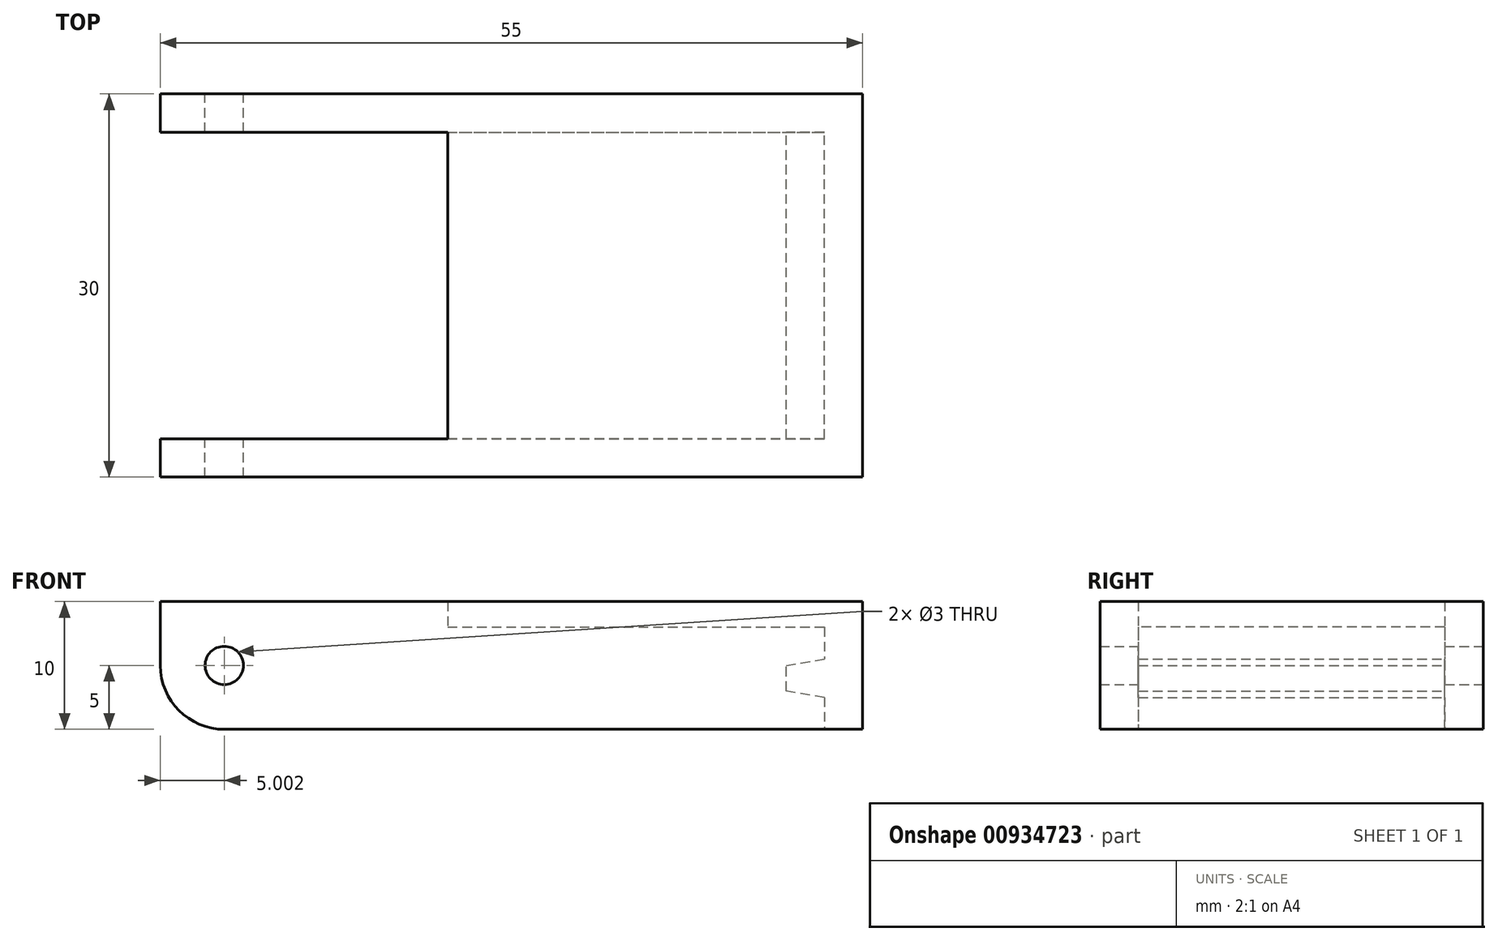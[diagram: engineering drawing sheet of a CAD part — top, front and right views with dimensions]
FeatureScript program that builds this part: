
annotation { "Feature Type Name" : "Feature", "Feature Type Description" : "" }
export const myFeature = defineFeature(function(context is Context, id is Id, definition is map)
    precondition{}
    {
        {
            var Q0;
            Q0=qCreatedBy(makeId("Top.planeOp"),FACE);
            var sketch = newSketch(context, id + "F0", { "sketchPlane" : qUnion([Q0])});
            skLineSegment(sketch, "E0", {"start": v(-28.72, -17.3) * mm, "end": v(26.28, -17.3) * mm});
            skLineSegment(sketch, "E1", {"start": v(26.28, -17.3) * mm, "end": v(26.28, 12.7) * mm});
            skLineSegment(sketch, "E2", {"start": v(26.28, 12.7) * mm, "end": v(-28.72, 12.7) * mm});
            skLineSegment(sketch, "E3", {"start": v(-28.72, 12.7) * mm, "end": v(-28.72, 9.7) * mm});
            skLineSegment(sketch, "E4", {"start": v(-28.72, 9.7) * mm, "end": v(-6.22, 9.7) * mm});
            skLineSegment(sketch, "E5", {"start": v(-6.22, 9.7) * mm, "end": v(-6.22, -14.3) * mm});
            skLineSegment(sketch, "E6", {"start": v(-6.22, -14.3) * mm, "end": v(-28.72, -14.3) * mm});
            skLineSegment(sketch, "E7", {"start": v(-28.72, -14.3) * mm, "end": v(-28.72, -17.3) * mm});
            skSolve(sketch);
        }
        {
            var Q0;
            Q0 = qSketchRegion(id + "F0", true);
            extrude(context, id + "F1", {"entities" : qUnion([Q0]), "depth" : 10 * mm, "offsetDistance" : 25 * mm});
        }
        {
            var Q0;
            Q0=makeQuery(id+"F1.opExtrude","CAP_FACE",FACE,{"disambiguationData":[OSD([sQuery(id+"F0.wireOp",EDGE,"E0"),sQuery(id+"F0.wireOp",EDGE,"E1"),sQuery(id+"F0.wireOp",EDGE,"E2"),sQuery(id+"F0.wireOp",EDGE,"E3"),sQuery(id+"F0.wireOp",EDGE,"E4"),sQuery(id+"F0.wireOp",EDGE,"E5"),sQuery(id+"F0.wireOp",EDGE,"E6"),sQuery(id+"F0.wireOp",EDGE,"E7")])],"isStart":true});
            var sketch = newSketch(context, id + "F2", { "sketchPlane" : qUnion([Q0])});
            skLineSegment(sketch, "E8.0", {"start": v(-28.72, 14.3) * mm, "end": v(26.28, 14.3) * mm, "construction": true});
            skLineSegment(sketch, "E9.0", {"start": v(26.28, -9.7) * mm, "end": v(-28.72, -9.7) * mm, "construction": true});
            skLineSegment(sketch, "E10.0", {"start": v(23.28, 17.3) * mm, "end": v(23.28, -12.7) * mm, "construction": true});
            skLineSegment(sketch, "E11.bottom", {"start": v(-6.22, 14.3) * mm, "end": v(23.28, 14.3) * mm});
            skLineSegment(sketch, "E11.top", {"start": v(-6.22, -9.7) * mm, "end": v(23.28, -9.7) * mm});
            skLineSegment(sketch, "E11.left", {"start": v(-6.22, 14.3) * mm, "end": v(-6.22, -9.7) * mm});
            skLineSegment(sketch, "E11.right", {"start": v(23.28, 14.3) * mm, "end": v(23.28, -9.7) * mm});
            skSolve(sketch);
        }
        {
            var Q0;
            Q0 = qSketchRegion(id + "F2", true);
            extrude(context, id + "F3", {"entities" : qUnion([Q0]), "operationType" : NewBodyOperationType.REMOVE, "oppositeDirection" : true, "depth" : 8 * mm, "offsetDistance" : 25 * mm});
        }
        {
            var Q0;
            Q0=makeQuery(id+"F3.boolean.opBoolean","MERGE",FACE,{"derivedFrom":[makeQuery(id+"F1.opExtrude","SWEPT_FACE",FACE,{"disambiguationData":[OSD([sQuery(id+"F0.wireOp",EDGE,"E4")])]})],"fromTools":[makeQuery(id+"F3.opExtrude","SWEPT_FACE",FACE,{"disambiguationData":[OSD([sQuery(id+"F2.wireOp",EDGE,"E11.top")])]})]});
            var sketch = newSketch(context, id + "F4", { "sketchPlane" : qUnion([Q0])});
            skLineSegment(sketch, "E12", {"start": v(23.28, 0) * mm, "end": v(17.27, 0) * mm, "construction": true});
            skLineSegment(sketch, "E13", {"start": v(23.28, 5.5) * mm, "end": v(23.28, 2.5) * mm});
            skLineSegment(sketch, "E14", {"start": v(23.28, 2.5) * mm, "end": v(20.28, 3) * mm});
            skLineSegment(sketch, "E15", {"start": v(20.28, 3) * mm, "end": v(20.28, 5) * mm});
            skLineSegment(sketch, "E16", {"start": v(20.28, 5) * mm, "end": v(23.28, 5.5) * mm});
            skSolve(sketch);
        }
        {
            var Q0;
            Q0 = qSketchRegion(id + "F4", true);
            extrude(context, id + "F5", {"entities" : qUnion([Q0]), "operationType" : NewBodyOperationType.ADD, "depth" : 24 * mm, "offsetDistance" : 25 * mm});
        }
        {
            var Q0;
            Q0=makeQuery(id+"F1.opExtrude","SWEPT_FACE",FACE,{"disambiguationData":[OSD([sQuery(id+"F0.wireOp",EDGE,"E2")])]});
            var sketch = newSketch(context, id + "F6", { "sketchPlane" : qUnion([Q0])});
            skLineSegment(sketch, "E17.bottom", {"start": v(28.72, 10) * mm, "end": v(16.6, 10) * mm, "construction": true});
            skLineSegment(sketch, "E17.top", {"start": v(28.72, 0) * mm, "end": v(16.6, 0) * mm, "construction": true});
            skLineSegment(sketch, "E17.left", {"start": v(28.72, 10) * mm, "end": v(28.72, 0) * mm, "construction": true});
            skCircle(sketch, "E18", {"center": v(23.72, 5) * mm, "radius": 1.5 * mm});
            skSolve(sketch);
        }
        {
            var Q0;
            Q0 = qSketchRegion(id + "F6", true);
            extrude(context, id + "F7", {"entities" : qUnion([Q0]), "operationType" : NewBodyOperationType.REMOVE, "oppositeDirection" : true, "depth" : 30 * mm, "offsetDistance" : 25 * mm});
        }
        {
            var Q0;
            Q0=makeQuery(id+"F1.opExtrude","CAP_EDGE",EDGE,{"disambiguationData":[OSD([sQuery(id+"F0.wireOp",EDGE,"E3")])],"isStart":true});
            var Q1;
            Q1=makeQuery(id+"F1.opExtrude","CAP_EDGE",EDGE,{"disambiguationData":[OSD([sQuery(id+"F0.wireOp",EDGE,"E7")])],"isStart":true});
            fillet(context, id + "F8", {"entities" : qUnion([Q0, Q1]), "radius" : 5 * mm, "tangentPropagation" : true, "allowEdgeOverflow" : false});
        }
    });
